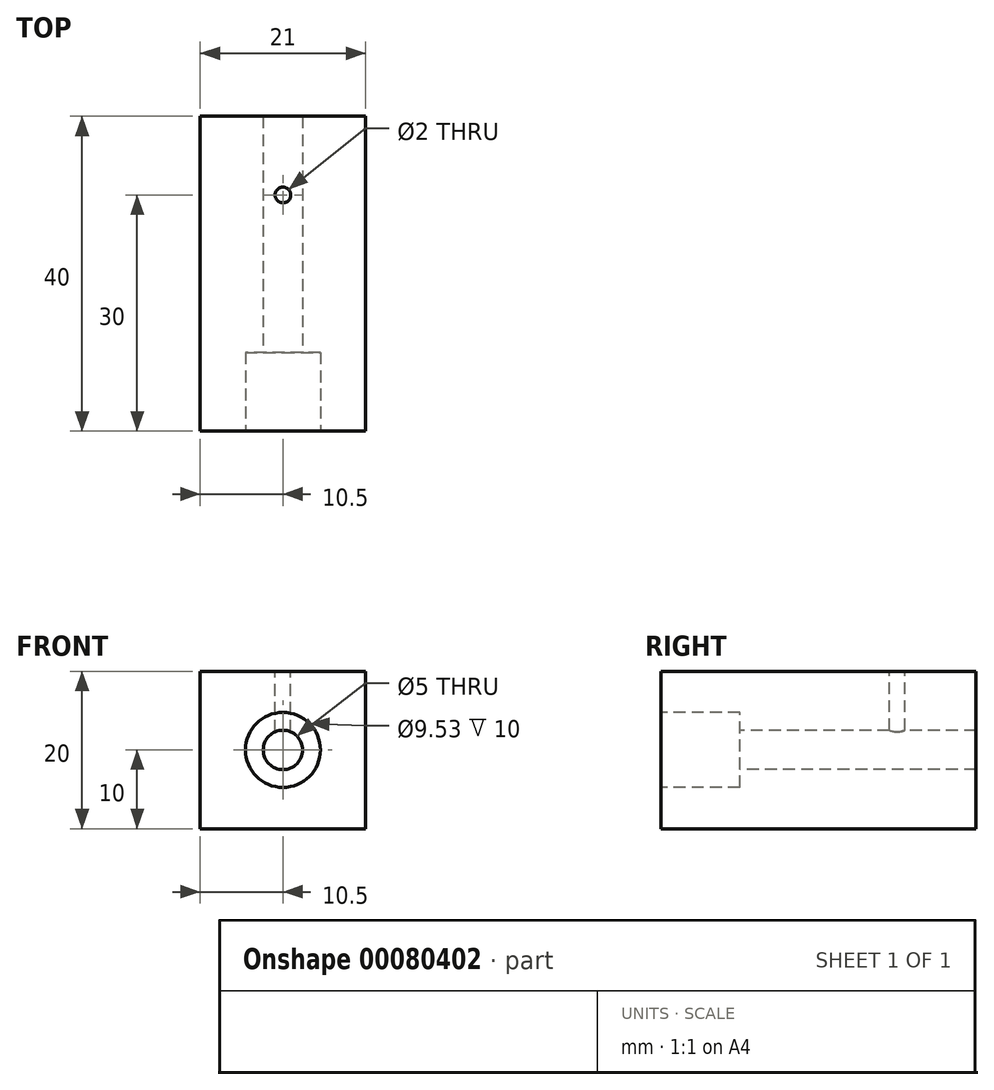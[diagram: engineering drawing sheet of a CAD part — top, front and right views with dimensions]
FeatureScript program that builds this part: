
annotation { "Feature Type Name" : "Feature", "Feature Type Description" : "" }
export const myFeature = defineFeature(function(context is Context, id is Id, definition is map)
    precondition{}
    {
        {
            var Q0;
            Q0=qCreatedBy(makeId("Front.planeOp"),FACE);
            var sketch = newSketch(context, id + "F0", { "sketchPlane" : qUnion([Q0])});
            skLineSegment(sketch, "E0.rect.bottom", {"start": v(10.5, 10) * mm, "end": v(-10.5, 10) * mm});
            skLineSegment(sketch, "E0.rect.top", {"start": v(10.5, -10) * mm, "end": v(-10.5, -10) * mm});
            skLineSegment(sketch, "E0.rect.left", {"start": v(10.5, 10) * mm, "end": v(10.5, -10) * mm});
            skLineSegment(sketch, "E0.rect.right", {"start": v(-10.5, 10) * mm, "end": v(-10.5, -10) * mm});
            skPoint(sketch, "E0.rect.middle", {"position": v(0, 0) * mm});
            skSolve(sketch);
        }
        {
            var Q0;
            Q0=makeQuery(id+"F0.imprint","IMPRINT",FACE,{"disambiguationData":[TD([[makeQuery(id+"F0.imprint","IMPRINT",EDGE,{"derivedFrom":sQuery(id+"F0.wireOp",EDGE,"E0.rect.bottom")}),1.0]])]});
            extrude(context, id + "F1", {"entities" : qUnion([Q0]), "oppositeDirection" : true, "depth" : 40 * mm});
        }
        {
            var Q0;
            Q0=qCreatedBy(makeId("Front.planeOp"),FACE);
            var sketch = newSketch(context, id + "F2", { "sketchPlane" : qUnion([Q0])});
            skCircle(sketch, "E1", {"center": v(0, 0) * mm, "radius": 2.5 * mm});
            skSolve(sketch);
        }
        {
            var Q0;
            Q0=makeQuery(id+"F2.imprint","IMPRINT",FACE,{"disambiguationData":[TD([[makeQuery(id+"F2.imprint","IMPRINT",EDGE,{"derivedFrom":sQuery(id+"F2.wireOp",EDGE,"E1")}),1.0]])]});
            extrude(context, id + "F3", {"entities" : qUnion([Q0]), "operationType" : NewBodyOperationType.REMOVE, "oppositeDirection" : true, "depth" : 30 * mm});
        }
        {
            var Q0;
            Q0=makeQuery(id+"F1.opExtrude","CAP_FACE",FACE,{"disambiguationData":[OSD([sQuery(id+"F0.wireOp",EDGE,"E0.rect.bottom"),sQuery(id+"F0.wireOp",EDGE,"E0.rect.top"),sQuery(id+"F0.wireOp",EDGE,"E0.rect.left"),sQuery(id+"F0.wireOp",EDGE,"E0.rect.right")])],"isStart":false});
            var sketch = newSketch(context, id + "F4", { "sketchPlane" : qUnion([Q0])});
            skCircle(sketch, "E2", {"center": v(0, 0) * mm, "radius": 2.5 * mm});
            skSolve(sketch);
        }
        {
            var Q0;
            Q0=makeQuery(id+"F4.imprint","IMPRINT",FACE,{"disambiguationData":[TD([[makeQuery(id+"F4.imprint","IMPRINT",EDGE,{"derivedFrom":sQuery(id+"F4.wireOp",EDGE,"E2")}),1.0]])]});
            extrude(context, id + "F5", {"entities" : qUnion([Q0]), "operationType" : NewBodyOperationType.REMOVE, "oppositeDirection" : true, "depth" : 10 * mm});
        }
        {
            var Q0;
            Q0=makeQuery(id+"F2.imprint","IMPRINT",FACE,{"disambiguationData":[TD([[makeQuery(id+"F2.imprint","IMPRINT",EDGE,{"derivedFrom":sQuery(id+"F2.wireOp",EDGE,"E1")}),1.0]])]});
            var sketch = newSketch(context, id + "F6", { "sketchPlane" : qUnion([Q0])});
            skCircle(sketch, "E3", {"center": v(0, 0) * mm, "radius": 4.76 * mm});
            skSolve(sketch);
        }
        {
            var Q0;
            Q0 = qSketchRegion(id + "F6", true);
            extrude(context, id + "F7", {"entities" : qUnion([Q0]), "operationType" : NewBodyOperationType.REMOVE, "oppositeDirection" : true, "depth" : 10 * mm});
        }
        {
            var Q0;
            Q0=makeQuery(id+"F1.opExtrude","SWEPT_FACE",FACE,{"disambiguationData":[OSD([sQuery(id+"F0.wireOp",EDGE,"E0.rect.bottom")])]});
            var sketch = newSketch(context, id + "F8", { "sketchPlane" : qUnion([Q0])});
            skLineSegment(sketch, "E4", {"start": v(0, 0) * mm, "end": v(0, 30) * mm});
            skCircle(sketch, "E5", {"center": v(0, 30) * mm, "radius": 1 * mm});
            skSolve(sketch);
        }
        {
            var Q0;
            Q0=makeQuery(id+"F8.imprint","IMPRINT",FACE,{"disambiguationData":[TD([[makeQuery(id+"F8.imprint","IMPRINT",EDGE,{"derivedFrom":sQuery(id+"F8.wireOp",EDGE,"E5")}),1.0]])]});
            extrude(context, id + "F9", {"entities" : qUnion([Q0]), "operationType" : NewBodyOperationType.REMOVE, "oppositeDirection" : true, "depth" : 10 * mm});
        }
    });
